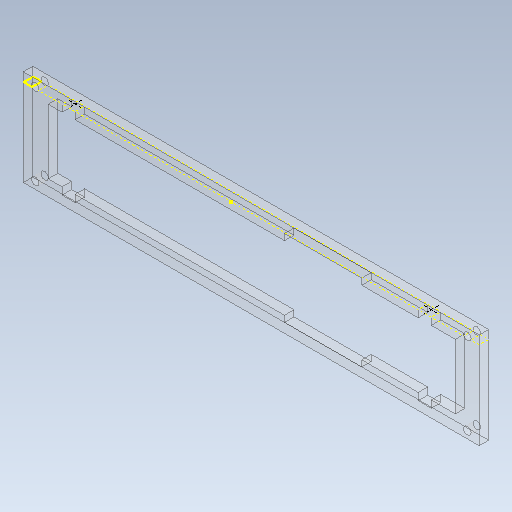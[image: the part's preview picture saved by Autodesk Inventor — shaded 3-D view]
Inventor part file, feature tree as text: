
AUTODESK INVENTOR PART (.ipt)
format: ipt  version: 2021 (Build 250183000, 183)  size: 175,104 bytes
history: native  units: mm
features: sketch x3, extrude x2, projected_geometry x1
ambient origin geometry x8: Origin, YZ Plane, XZ Plane, XY Plane, X Axis, Y Axis, Z Axis, Center Point
bodies: Solid1 (feature_tree)
feature tree (6):
  extrude  "Extrusion1"  Depth=4.0mm
  extrude  "Extrusion2"  Depth=40.4mm
  sketch  "Sketch4"  dims[d5=82.0mm d6=4.0mm d7=0.0mm d8=5.5mm d9=6.0mm d10=5.5mm d11=6.0mm d12=5.5mm d13=6.0mm d14=5.5mm d15=6.0mm d16=4.0mm d17=0.0mm d18=5.0mm d19=5.0mm d20=3.0mm d21=3.0mm d22=5.0mm d23=3.0mm d24=5.0mm d25=3.0mm d26=2.75mm d27=2.75mm]
  sketch  "Sketch1"  dims[d0=1.0mm d1=4.0mm]
  sketch  "Sketch2"  dims[d2=110.0mm d3=40.4mm]
  projected_geometry  "Project Cut Edges1"
